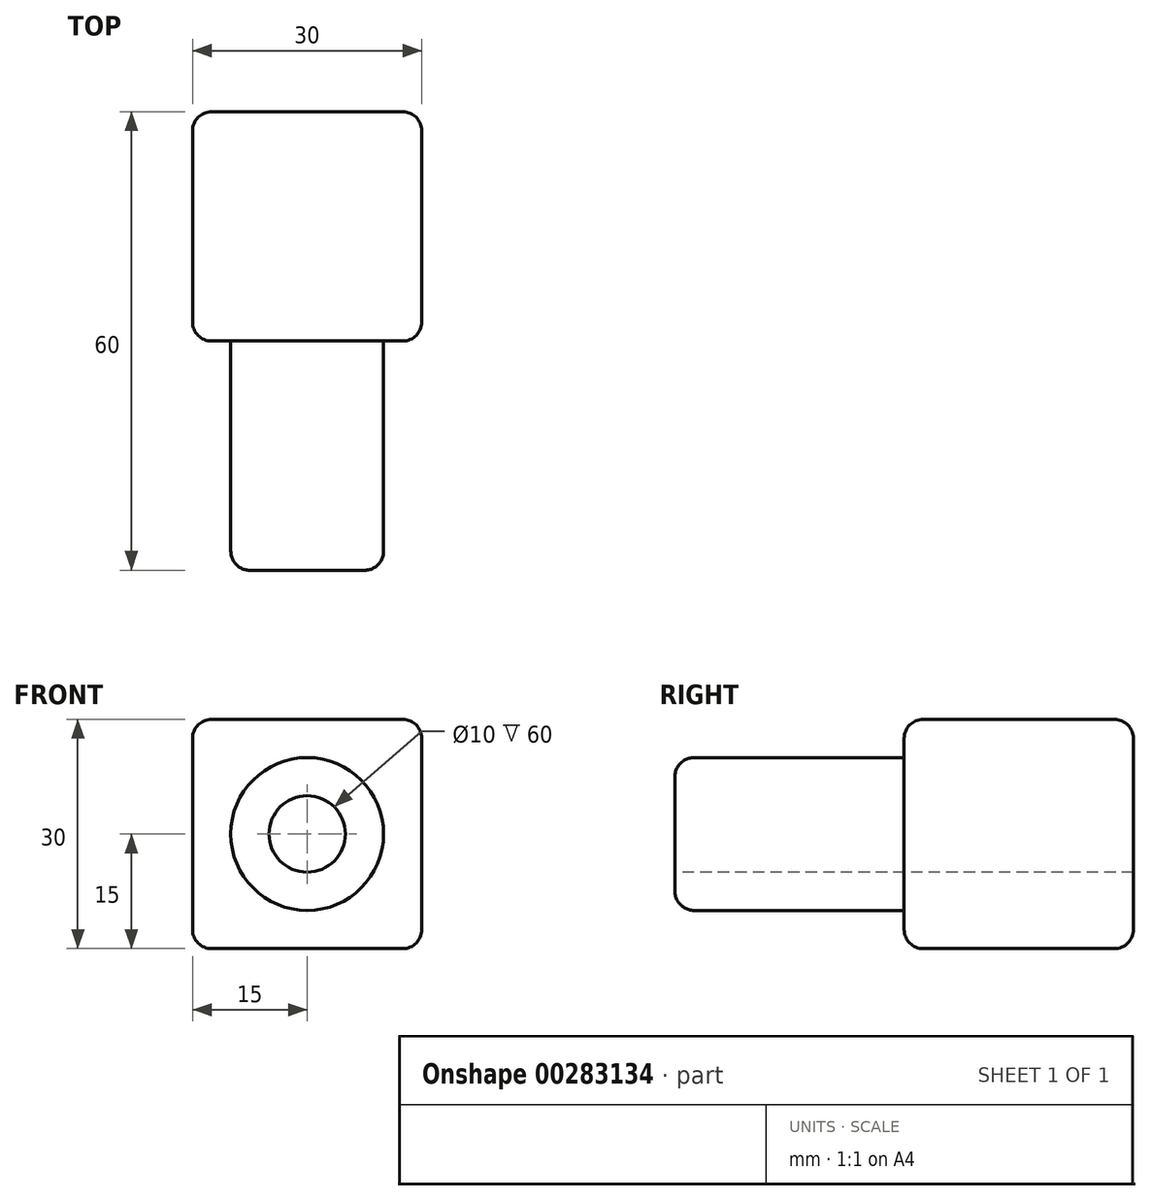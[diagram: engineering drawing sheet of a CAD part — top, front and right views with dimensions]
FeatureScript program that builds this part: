
annotation { "Feature Type Name" : "Feature", "Feature Type Description" : "" }
export const myFeature = defineFeature(function(context is Context, id is Id, definition is map)
    precondition{}
    {
        {
            var Q0;
            Q0=qCreatedBy(makeId("Front.planeOp"),FACE);
            var sketch = newSketch(context, id + "F0", { "sketchPlane" : qUnion([Q0])});
            skLineSegment(sketch, "E0.bottom", {"start": v(15, 15) * mm, "end": v(-15, 15) * mm});
            skLineSegment(sketch, "E0.top", {"start": v(15, -15) * mm, "end": v(-15, -15) * mm});
            skLineSegment(sketch, "E0.left", {"start": v(15, 15) * mm, "end": v(15, -15) * mm});
            skLineSegment(sketch, "E0.right", {"start": v(-15, 15) * mm, "end": v(-15, -15) * mm});
            skPoint(sketch, "E0.middle", {"position": v(0, 0) * mm});
            skSolve(sketch);
        }
        {
            var Q0;
            Q0 = qSketchRegion(id + "F0", true);
            extrude(context, id + "F1", {"entities" : qUnion([Q0]), "depth" : 30 * mm});
        }
        {
            var Q0;
            Q0=makeQuery(id+"F1.opExtrude","CAP_FACE",FACE,{"disambiguationData":[OSD([sQuery(id+"F0.wireOp",EDGE,"E0.bottom"),sQuery(id+"F0.wireOp",EDGE,"E0.top"),sQuery(id+"F0.wireOp",EDGE,"E0.left"),sQuery(id+"F0.wireOp",EDGE,"E0.right")])],"isStart":false});
            var sketch = newSketch(context, id + "F2", { "sketchPlane" : qUnion([Q0])});
            skCircle(sketch, "E1", {"center": v(0, 0) * mm, "radius": 10 * mm});
            skSolve(sketch);
        }
        {
            var Q0;
            Q0 = qSketchRegion(id + "F2", true);
            extrude(context, id + "F3", {"entities" : qUnion([Q0]), "operationType" : NewBodyOperationType.ADD, "depth" : 30 * mm});
        }
        {
            var Q0;
            Q0=makeQuery(id+"F1.opExtrude","CAP_EDGE",EDGE,{"disambiguationData":[OSD([sQuery(id+"F0.wireOp",EDGE,"E0.bottom")])],"isStart":false});
            var Q1;
            Q1=makeQuery(id+"F1.opExtrude","CAP_EDGE",EDGE,{"disambiguationData":[OSD([sQuery(id+"F0.wireOp",EDGE,"E0.right")])],"isStart":false});
            var Q2;
            Q2=makeQuery(id+"F1.opExtrude","CAP_EDGE",EDGE,{"disambiguationData":[OSD([sQuery(id+"F0.wireOp",EDGE,"E0.top")])],"isStart":false});
            var Q3;
            Q3=makeQuery(id+"F1.opExtrude","CAP_EDGE",EDGE,{"disambiguationData":[OSD([sQuery(id+"F0.wireOp",EDGE,"E0.left")])],"isStart":false});
            var Q4;
            Q4=makeQuery(id+"F3.opExtrude","CAP_EDGE",EDGE,{"disambiguationData":[OSD([sQuery(id+"F2.wireOp",EDGE,"E1")])],"isStart":false});
            var Q5;
            Q5=makeQuery(id+"F1.opExtrude","SWEPT_EDGE",EDGE,{"disambiguationData":[OSD([sQuery(id+"F0.wireOp",EDGE,"E0.bottom"),sQuery(id+"F0.wireOp",EDGE,"E0.right")])]});
            var Q6;
            Q6=makeQuery(id+"F1.opExtrude","SWEPT_EDGE",EDGE,{"disambiguationData":[OSD([sQuery(id+"F0.wireOp",EDGE,"E0.top"),sQuery(id+"F0.wireOp",EDGE,"E0.right")])]});
            var Q7;
            Q7=makeQuery(id+"F1.opExtrude","CAP_EDGE",EDGE,{"disambiguationData":[OSD([sQuery(id+"F0.wireOp",EDGE,"E0.right")])],"isStart":true});
            var Q8;
            Q8=makeQuery(id+"F1.opExtrude","SWEPT_EDGE",EDGE,{"disambiguationData":[OSD([sQuery(id+"F0.wireOp",EDGE,"E0.bottom"),sQuery(id+"F0.wireOp",EDGE,"E0.left")])]});
            var Q9;
            Q9=makeQuery(id+"F1.opExtrude","SWEPT_EDGE",EDGE,{"disambiguationData":[OSD([sQuery(id+"F0.wireOp",EDGE,"E0.top"),sQuery(id+"F0.wireOp",EDGE,"E0.left")])]});
            var Q10;
            Q10=makeQuery(id+"F1.opExtrude","CAP_EDGE",EDGE,{"disambiguationData":[OSD([sQuery(id+"F0.wireOp",EDGE,"E0.left")])],"isStart":true});
            var Q11;
            Q11=makeQuery(id+"F1.opExtrude","CAP_EDGE",EDGE,{"disambiguationData":[OSD([sQuery(id+"F0.wireOp",EDGE,"E0.bottom")])],"isStart":true});
            var Q12;
            Q12=makeQuery(id+"F1.opExtrude","CAP_EDGE",EDGE,{"disambiguationData":[OSD([sQuery(id+"F0.wireOp",EDGE,"E0.top")])],"isStart":true});
            fillet(context, id + "F4", {"entities" : qUnion([Q0, Q1, Q2, Q3, Q4, Q5, Q6, Q7, Q8, Q9, Q10, Q11, Q12]), "radius" : 2.5 * mm, "tangentPropagation" : true, "allowEdgeOverflow" : false});
        }
        {
            var Q0;
            Q0=makeQuery(id+"F3.opExtrude","CAP_FACE",FACE,{"disambiguationData":[OSD([sQuery(id+"F2.wireOp",EDGE,"E1")])],"isStart":false});
            var sketch = newSketch(context, id + "F5", { "sketchPlane" : qUnion([Q0])});
            skCircle(sketch, "E2", {"center": v(0, 0) * mm, "radius": 5 * mm});
            skSolve(sketch);
        }
        {
            var Q0;
            Q0=makeQuery(id+"F5.imprint","IMPRINT",FACE,{"disambiguationData":[TD([[makeQuery(id+"F5.imprint","IMPRINT",EDGE,{"derivedFrom":sQuery(id+"F5.wireOp",EDGE,"E2")}),1.0]])]});
            extrude(context, id + "F6", {"entities" : qUnion([Q0]), "operationType" : NewBodyOperationType.REMOVE, "endBound" : BoundingType.THROUGH_ALL, "oppositeDirection" : true, "depth" : 25 * mm});
        }
    });
